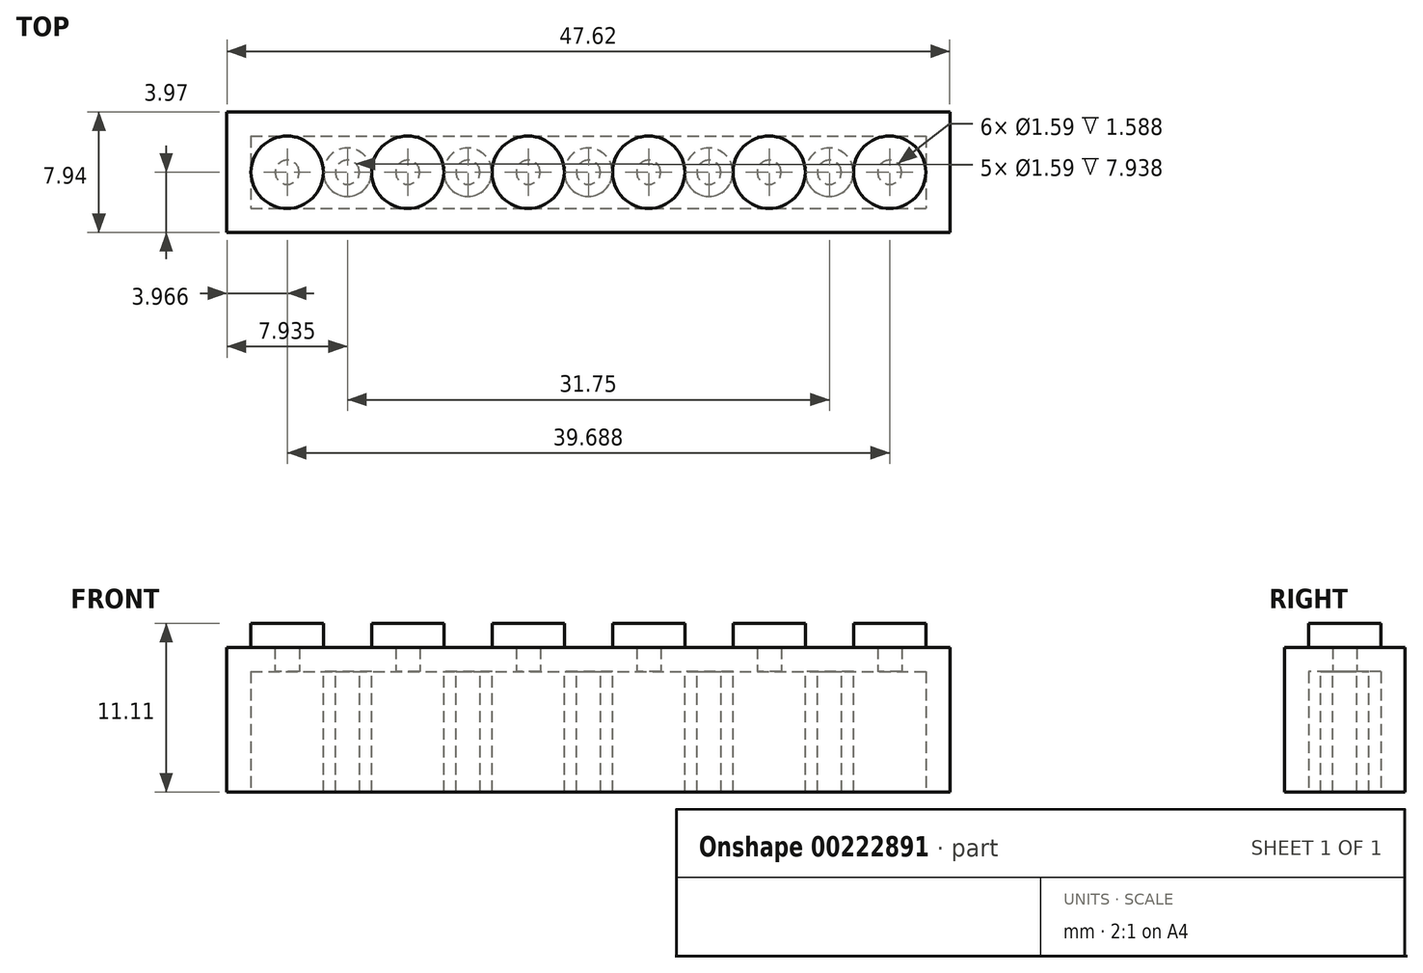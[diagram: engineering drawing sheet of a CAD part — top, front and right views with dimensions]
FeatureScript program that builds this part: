
annotation { "Feature Type Name" : "Feature", "Feature Type Description" : "" }
export const myFeature = defineFeature(function(context is Context, id is Id, definition is map)
    precondition{}
    {
        {
            var Q0;
            Q0=qCreatedBy(makeId("Top.planeOp"),FACE);
            var sketch = newSketch(context, id + "F0", { "sketchPlane" : qUnion([Q0])});
            skLineSegment(sketch, "E0.bottom", {"start": v(-23.81, 3.97) * mm, "end": v(23.81, 3.97) * mm});
            skLineSegment(sketch, "E0.top", {"start": v(-23.81, -3.97) * mm, "end": v(23.81, -3.97) * mm});
            skLineSegment(sketch, "E0.left", {"start": v(-23.81, 3.97) * mm, "end": v(-23.81, -3.97) * mm});
            skLineSegment(sketch, "E0.right", {"start": v(23.81, 3.97) * mm, "end": v(23.81, -3.97) * mm});
            skPoint(sketch, "E0.middle", {"position": v(0, 0) * mm});
            skCircle(sketch, "E1", {"center": v(-19.84, 0) * mm, "radius": 2.38 * mm});
            skCircle(sketch, "E2.1.0.0", {"center": v(-11.9, 0) * mm, "radius": 2.38 * mm});
            skCircle(sketch, "E2.2.0.0", {"center": v(-3.97, 0) * mm, "radius": 2.38 * mm});
            skCircle(sketch, "E2.3.0.0", {"center": v(3.97, 0) * mm, "radius": 2.38 * mm});
            skLineSegment(sketch, "E2.direction1", {"start": v(-19.84, 0) * mm, "end": v(-11.9, 0) * mm, "construction": true});
            skCircle(sketch, "E3.0.4.0", {"center": v(11.9, 0) * mm, "radius": 2.38 * mm});
            skCircle(sketch, "E3.0.5.0", {"center": v(19.84, 0) * mm, "radius": 2.38 * mm});
            skSolve(sketch);
        }
        {
            var Q0;
            Q0=makeQuery(id+"F0.imprint","IMPRINT",FACE,{"disambiguationData":[TD([[makeQuery(id+"F0.imprint","IMPRINT",EDGE,{"derivedFrom":sQuery(id+"F0.wireOp",EDGE,"E0.bottom")}),-1.0]])]});
            extrude(context, id + "F1", {"entities" : qUnion([Q0]), "depth" : 9.52 * mm});
        }
        {
            var Q0;
            Q0=makeQuery(id+"F0.imprint","IMPRINT",FACE,{"disambiguationData":[TD([[makeQuery(id+"F0.imprint","IMPRINT",EDGE,{"derivedFrom":sQuery(id+"F0.wireOp",EDGE,"8b71ed98-f0e1-4300-85cb-82ad82c44b3e0.MirrorC")}),-1.0]])]});
            var Q1;
            Q1=makeQuery(id+"F0.imprint","IMPRINT",FACE,{"disambiguationData":[TD([[makeQuery(id+"F0.imprint","IMPRINT",EDGE,{"derivedFrom":sQuery(id+"F0.wireOp",EDGE,"E1")}),1.0]])]});
            var Q2;
            Q2=makeQuery(id+"F0.imprint","IMPRINT",FACE,{"disambiguationData":[TD([[makeQuery(id+"F0.imprint","IMPRINT",EDGE,{"derivedFrom":sQuery(id+"F0.wireOp",EDGE,"E2.1.0.0")}),1.0]])]});
            var Q3;
            Q3=makeQuery(id+"F0.imprint","IMPRINT",FACE,{"disambiguationData":[TD([[makeQuery(id+"F0.imprint","IMPRINT",EDGE,{"derivedFrom":sQuery(id+"F0.wireOp",EDGE,"E2.2.0.0")}),1.0]])]});
            var Q4;
            Q4=makeQuery(id+"F0.imprint","IMPRINT",FACE,{"disambiguationData":[TD([[makeQuery(id+"F0.imprint","IMPRINT",EDGE,{"derivedFrom":sQuery(id+"F0.wireOp",EDGE,"E2.3.0.0")}),1.0]])]});
            var Q5;
            Q5=makeQuery(id+"F0.imprint","IMPRINT",FACE,{"disambiguationData":[TD([[makeQuery(id+"F0.imprint","IMPRINT",EDGE,{"derivedFrom":sQuery(id+"F0.wireOp",EDGE,"E3.0.4.0")}),1.0]])]});
            var Q6;
            Q6=makeQuery(id+"F0.imprint","IMPRINT",FACE,{"disambiguationData":[TD([[makeQuery(id+"F0.imprint","IMPRINT",EDGE,{"derivedFrom":sQuery(id+"F0.wireOp",EDGE,"E3.0.5.0")}),1.0]])]});
            var Q7;
            Q7=makeQuery(id+"F0.imprint","IMPRINT",FACE,{"disambiguationData":[TD([[makeQuery(id+"F0.imprint","IMPRINT",EDGE,{"derivedFrom":sQuery(id+"F0.wireOp",EDGE,"958e86d0-05e2-43b9-828d-42b0878e5e54.0.6.0")}),1.0]])]});
            var Q8;
            Q8=makeQuery(id+"F0.imprint","IMPRINT",FACE,{"disambiguationData":[TD([[makeQuery(id+"F0.imprint","IMPRINT",EDGE,{"derivedFrom":sQuery(id+"F0.wireOp",EDGE,"958e86d0-05e2-43b9-828d-42b0878e5e54.0.7.0")}),1.0]])]});
            var Q9;
            Q9=makeQuery(id+"F0.imprint","IMPRINT",FACE,{"disambiguationData":[TD([[makeQuery(id+"F0.imprint","IMPRINT",EDGE,{"derivedFrom":sQuery(id+"F0.wireOp",EDGE,"958e86d0-05e2-43b9-828d-42b0878e5e54.0.8.0")}),1.0]])]});
            var Q10;
            Q10=makeQuery(id+"F0.imprint","IMPRINT",FACE,{"disambiguationData":[TD([[makeQuery(id+"F0.imprint","IMPRINT",EDGE,{"derivedFrom":sQuery(id+"F0.wireOp",EDGE,"958e86d0-05e2-43b9-828d-42b0878e5e54.0.9.0")}),1.0]])]});
            var Q11;
            Q11=makeQuery(id+"F0.imprint","IMPRINT",FACE,{"disambiguationData":[TD([[makeQuery(id+"F0.imprint","IMPRINT",EDGE,{"derivedFrom":sQuery(id+"F0.wireOp",EDGE,"958e86d0-05e2-43b9-828d-42b0878e5e54.0.10.0")}),1.0]])]});
            var Q12;
            Q12=makeQuery(id+"F0.imprint","IMPRINT",FACE,{"disambiguationData":[TD([[makeQuery(id+"F0.imprint","IMPRINT",EDGE,{"derivedFrom":sQuery(id+"F0.wireOp",EDGE,"958e86d0-05e2-43b9-828d-42b0878e5e54.0.11.0")}),1.0]])]});
            extrude(context, id + "F2", {"entities" : qUnion([Q0, Q1, Q2, Q3, Q4, Q5, Q6, Q7, Q8, Q9, Q10, Q11, Q12]), "operationType" : NewBodyOperationType.ADD, "depth" : 11.1 * mm});
        }
        {
            var Q0;
            {var subQ0=sQuery(id+"F0.wireOp",EDGE,"8b71ed98-f0e1-4300-85cb-82ad82c44b3e0.MirrorC");var subQ1=sQuery(id+"F0.wireOp",EDGE,"E1");Q0=makeQuery(id+"F2.boolean.opBoolean","MERGE",FACE,{"derivedFrom":[makeQuery(id+"F1.opExtrude","CAP_FACE",FACE,{"disambiguationData":[OSD([sQuery(id+"F0.wireOp",EDGE,"E0.bottom"),sQuery(id+"F0.wireOp",EDGE,"E0.top"),sQuery(id+"F0.wireOp",EDGE,"E0.left"),sQuery(id+"F0.wireOp",EDGE,"E0.right"),subQ1,subQ0])],"isStart":true}),makeQuery(id+"F2.opExtrude","CAP_FACE",FACE,{"disambiguationData":[OSD([subQ1])],"isStart":true}),makeQuery(id+"F2.opExtrude","CAP_FACE",FACE,{"disambiguationData":[OSD([subQ0])],"isStart":true})]});}
            shell(context, id + "F3", {"entities" : qUnion([Q0]), "thickness" : 1.59 * mm});
        }
        {
            var Q0;
            Q0=makeQuery(id+"F3.opShell","OFFSET_FACE",FACE,{"disambiguationData":[OSD([sQuery(id+"F0.wireOp",EDGE,"E0.bottom"),sQuery(id+"F0.wireOp",EDGE,"E0.top"),sQuery(id+"F0.wireOp",EDGE,"E0.left"),sQuery(id+"F0.wireOp",EDGE,"E0.right"),sQuery(id+"F0.wireOp",EDGE,"E1"),sQuery(id+"F0.wireOp",EDGE,"8b71ed98-f0e1-4300-85cb-82ad82c44b3e0.MirrorC")])]});
            var sketch = newSketch(context, id + "F4", { "sketchPlane" : qUnion([Q0])});
            skCircle(sketch, "E4", {"center": v(-15.88, 0) * mm, "radius": 1.59 * mm});
            skCircle(sketch, "E5", {"center": v(-15.88, 0) * mm, "radius": 0.8 * mm});
            skLineSegment(sketch, "E6.direction1", {"start": v(-15.88, 0) * mm, "end": v(-7.94, 0) * mm, "construction": true});
            skCircle(sketch, "E7.0.1.0", {"center": v(-7.94, 0) * mm, "radius": 1.59 * mm});
            skCircle(sketch, "E7.2.1.0", {"center": v(-7.94, 0) * mm, "radius": 0.8 * mm});
            skCircle(sketch, "E7.0.2.0", {"center": v(0, 0) * mm, "radius": 1.59 * mm});
            skCircle(sketch, "E7.2.2.0", {"center": v(0, 0) * mm, "radius": 0.8 * mm});
            skCircle(sketch, "E7.0.3.0", {"center": v(7.94, 0) * mm, "radius": 1.59 * mm});
            skCircle(sketch, "E7.2.3.0", {"center": v(7.94, 0) * mm, "radius": 0.8 * mm});
            skCircle(sketch, "E7.0.4.0", {"center": v(15.87, 0) * mm, "radius": 1.59 * mm});
            skCircle(sketch, "E7.2.4.0", {"center": v(15.87, 0) * mm, "radius": 0.8 * mm});
            skSolve(sketch);
        }
        {
            var Q0;
            Q0=makeQuery(id+"F4.imprint","IMPRINT",FACE,{"disambiguationData":[TD([[makeQuery(id+"F4.imprint","IMPRINT",EDGE,{"derivedFrom":sQuery(id+"F4.wireOp",EDGE,"E4")}),1.0]])]});
            var Q1;
            Q1=makeQuery(id+"F4.imprint","IMPRINT",FACE,{"disambiguationData":[TD([[makeQuery(id+"F4.imprint","IMPRINT",EDGE,{"derivedFrom":sQuery(id+"F4.wireOp",EDGE,"E6.1.0.0")}),1.0]])]});
            var Q2;
            Q2=makeQuery(id+"F4.imprint","IMPRINT",FACE,{"disambiguationData":[TD([[makeQuery(id+"F4.imprint","IMPRINT",EDGE,{"derivedFrom":sQuery(id+"F4.wireOp",EDGE,"E6.2.0.0")}),1.0]])]});
            var Q3;
            Q3=makeQuery(id+"F4.imprint","IMPRINT",FACE,{"disambiguationData":[TD([[makeQuery(id+"F4.imprint","IMPRINT",EDGE,{"derivedFrom":sQuery(id+"F4.wireOp",EDGE,"085d88cb-4c62-47cd-8297-15103481ccae.0.3.0")}),1.0]])]});
            var Q4;
            Q4=makeQuery(id+"F4.imprint","IMPRINT",FACE,{"disambiguationData":[TD([[makeQuery(id+"F4.imprint","IMPRINT",EDGE,{"derivedFrom":sQuery(id+"F4.wireOp",EDGE,"085d88cb-4c62-47cd-8297-15103481ccae.0.4.0")}),1.0]])]});
            var Q5;
            Q5=makeQuery(id+"F4.imprint","IMPRINT",FACE,{"disambiguationData":[TD([[makeQuery(id+"F4.imprint","IMPRINT",EDGE,{"derivedFrom":sQuery(id+"F4.wireOp",EDGE,"E7.0.1.0")}),1.0]])]});
            var Q6;
            Q6=makeQuery(id+"F4.imprint","IMPRINT",FACE,{"disambiguationData":[TD([[makeQuery(id+"F4.imprint","IMPRINT",EDGE,{"derivedFrom":sQuery(id+"F4.wireOp",EDGE,"E7.0.2.0")}),1.0]])]});
            var Q7;
            Q7=makeQuery(id+"F4.imprint","IMPRINT",FACE,{"disambiguationData":[TD([[makeQuery(id+"F4.imprint","IMPRINT",EDGE,{"derivedFrom":sQuery(id+"F4.wireOp",EDGE,"E7.0.3.0")}),1.0]])]});
            var Q8;
            Q8=makeQuery(id+"F4.imprint","IMPRINT",FACE,{"disambiguationData":[TD([[makeQuery(id+"F4.imprint","IMPRINT",EDGE,{"derivedFrom":sQuery(id+"F4.wireOp",EDGE,"E7.0.4.0")}),1.0]])]});
            var Q9;
            Q9=makeQuery(id+"F4.imprint","IMPRINT",FACE,{"disambiguationData":[TD([[makeQuery(id+"F4.imprint","IMPRINT",EDGE,{"derivedFrom":sQuery(id+"F4.wireOp",EDGE,"E7.0.5.0")}),1.0]])]});
            var Q10;
            Q10=makeQuery(id+"F4.imprint","IMPRINT",FACE,{"disambiguationData":[TD([[makeQuery(id+"F4.imprint","IMPRINT",EDGE,{"derivedFrom":sQuery(id+"F4.wireOp",EDGE,"E7.0.6.0")}),1.0]])]});
            var Q11;
            Q11=makeQuery(id+"F4.imprint","IMPRINT",FACE,{"disambiguationData":[TD([[makeQuery(id+"F4.imprint","IMPRINT",EDGE,{"derivedFrom":sQuery(id+"F4.wireOp",EDGE,"E7.0.7.0")}),1.0]])]});
            var Q12;
            Q12=makeQuery(id+"F4.imprint","IMPRINT",FACE,{"disambiguationData":[TD([[makeQuery(id+"F4.imprint","IMPRINT",EDGE,{"derivedFrom":sQuery(id+"F4.wireOp",EDGE,"E7.0.8.0")}),1.0]])]});
            var Q13;
            Q13=makeQuery(id+"F4.imprint","IMPRINT",FACE,{"disambiguationData":[TD([[makeQuery(id+"F4.imprint","IMPRINT",EDGE,{"derivedFrom":sQuery(id+"F4.wireOp",EDGE,"E7.0.9.0")}),1.0]])]});
            var Q14;
            Q14=makeQuery(id+"F4.imprint","IMPRINT",FACE,{"disambiguationData":[TD([[makeQuery(id+"F4.imprint","IMPRINT",EDGE,{"derivedFrom":sQuery(id+"F4.wireOp",EDGE,"E7.0.10.0")}),1.0]])]});
            extrude(context, id + "F5", {"entities" : qUnion([Q0, Q1, Q2, Q3, Q4, Q5, Q6, Q7, Q8, Q9, Q10, Q11, Q12, Q13, Q14]), "operationType" : NewBodyOperationType.ADD, "depth" : 7.94 * mm});
        }
    });
